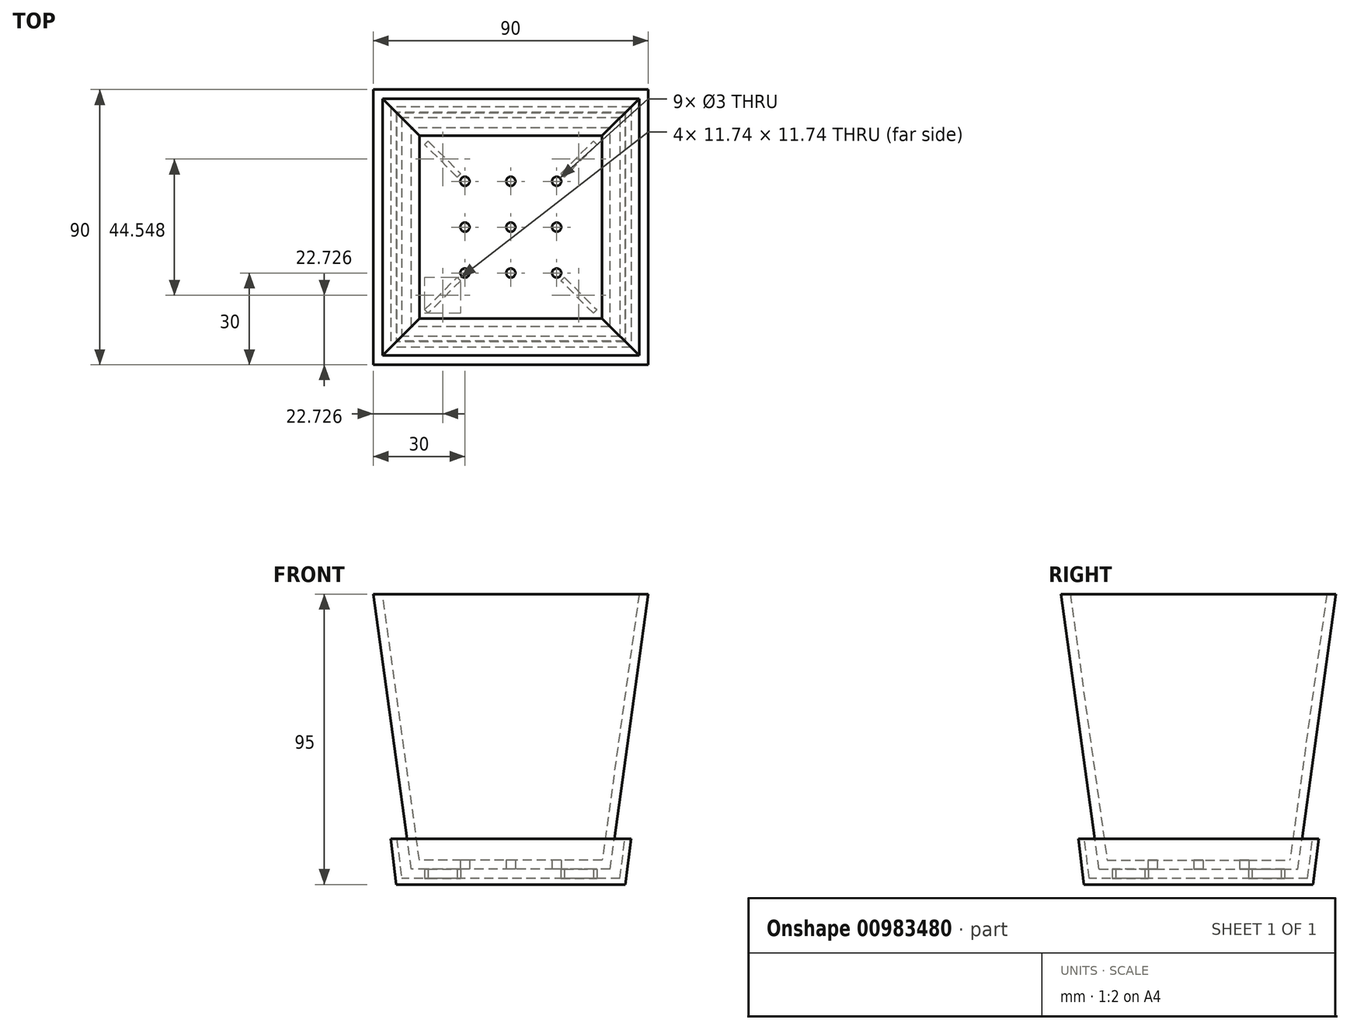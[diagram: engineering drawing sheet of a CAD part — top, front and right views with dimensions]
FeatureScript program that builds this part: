
annotation { "Feature Type Name" : "Feature", "Feature Type Description" : "" }
export const myFeature = defineFeature(function(context is Context, id is Id, definition is map)
    precondition{}
    {
        {
            var Q0;
            Q0=qCreatedBy(makeId("Top.planeOp"),FACE);
            var sketch = newSketch(context, id + "F0", { "sketchPlane" : qUnion([Q0])});
            skLineSegment(sketch, "E0.bottom", {"start": v(32.5, -32.5) * mm, "end": v(-32.5, -32.5) * mm});
            skLineSegment(sketch, "E0.top", {"start": v(32.5, 32.5) * mm, "end": v(-32.5, 32.5) * mm});
            skLineSegment(sketch, "E0.left", {"start": v(32.5, -32.5) * mm, "end": v(32.5, 32.5) * mm});
            skLineSegment(sketch, "E0.right", {"start": v(-32.5, -32.5) * mm, "end": v(-32.5, 32.5) * mm});
            skSolve(sketch);
        }
        {
            var Q0;
            Q0=qCreatedBy(makeId("Top.planeOp"),FACE);
            cPlane(context, id + "F1", {"entities" : qUnion([Q0]), "cplaneType" : CPlaneType.OFFSET, "offset" : 90 * mm, "width" : 150 * mm, "height" : 150 * mm});
        }
        {
            var Q0;
            Q0=qCreatedBy(id+"F1.planeOp",FACE);
            var sketch = newSketch(context, id + "F2", { "sketchPlane" : qUnion([Q0])});
            skLineSegment(sketch, "E1.bottom", {"start": v(45, -45) * mm, "end": v(-45, -45) * mm});
            skLineSegment(sketch, "E1.top", {"start": v(45, 45) * mm, "end": v(-45, 45) * mm});
            skLineSegment(sketch, "E1.left", {"start": v(45, -45) * mm, "end": v(45, 45) * mm});
            skLineSegment(sketch, "E1.right", {"start": v(-45, -45) * mm, "end": v(-45, 45) * mm});
            skPoint(sketch, "E1.middle", {"position": v(0, 0) * mm});
            skSolve(sketch);
        }
        {
            var Q0;
            Q0=makeQuery(id+"F0.imprint","IMPRINT",FACE,{"disambiguationData":[TD([[makeQuery(id+"F0.imprint","IMPRINT",EDGE,{"derivedFrom":sQuery(id+"F0.wireOp",EDGE,"E0.bottom")}),-1.0]])]});
            var Q1;
            Q1=makeQuery(id+"F2.imprint","IMPRINT",FACE,{"disambiguationData":[TD([[makeQuery(id+"F2.imprint","IMPRINT",EDGE,{"derivedFrom":sQuery(id+"F2.wireOp",EDGE,"E1.bottom")}),-1.0]])]});
            loft(context, id + "F3", {"sheetProfilesArray" : [{ "sheetProfileEntities" : qUnion([Q0]) }, { "sheetProfileEntities" : qUnion([Q1]) }]});
        }
        {
            var Q0;
            Q0=makeQuery(id+"F3.opLoft","CAP_FACE",FACE,{"disambiguationData":[OSD([makeQuery(id+"F2.imprint","IMPRINT",FACE,{"disambiguationData":[TD([[makeQuery(id+"F2.imprint","IMPRINT",EDGE,{"derivedFrom":sQuery(id+"F2.wireOp",EDGE,"E1.bottom")}),-1.0]])]})])],"isStart":true});
            shell(context, id + "F4", {"entities" : qUnion([Q0]), "thickness" : 3 * mm});
        }
        {
            var Q0;
            Q0=qCreatedBy(makeId("Top.planeOp"),FACE);
            var sketch = newSketch(context, id + "F5", { "sketchPlane" : qUnion([Q0])});
            skCircle(sketch, "E2", {"center": v(-15, -15) * mm, "radius": 1.5 * mm});
            skCircle(sketch, "E3.0.1.0", {"center": v(-15, 0) * mm, "radius": 1.5 * mm});
            skCircle(sketch, "E3.0.2.0", {"center": v(-15, 15) * mm, "radius": 1.5 * mm});
            skCircle(sketch, "E3.1.0.0", {"center": v(0, -15) * mm, "radius": 1.5 * mm});
            skCircle(sketch, "E3.1.1.0", {"center": v(0, 0) * mm, "radius": 1.5 * mm});
            skCircle(sketch, "E3.1.2.0", {"center": v(0, 15) * mm, "radius": 1.5 * mm});
            skCircle(sketch, "E3.2.0.0", {"center": v(15, -15) * mm, "radius": 1.5 * mm});
            skCircle(sketch, "E3.2.1.0", {"center": v(15, 0) * mm, "radius": 1.5 * mm});
            skCircle(sketch, "E3.2.2.0", {"center": v(15, 15) * mm, "radius": 1.5 * mm});
            skLineSegment(sketch, "E3.direction1", {"start": v(-15, -15) * mm, "end": v(0, -15) * mm, "construction": true});
            skLineSegment(sketch, "E3.direction2", {"start": v(-15, -15) * mm, "end": v(-15, 0) * mm, "construction": true});
            skSolve(sketch);
        }
        {
            var Q0;
            Q0 = qSketchRegion(id + "F5", true);
            extrude(context, id + "F6", {"entities" : qUnion([Q0]), "operationType" : NewBodyOperationType.REMOVE, "endBound" : BoundingType.THROUGH_ALL, "depth" : 25 * mm, "offsetDistance" : 25 * mm});
        }
        {
            var Q0;
            Q0=qCreatedBy(makeId("Top.planeOp"),FACE);
            cPlane(context, id + "F7", {"entities" : qUnion([Q0]), "cplaneType" : CPlaneType.OFFSET, "offset" : 5 * mm, "oppositeDirection" : true, "width" : 150 * mm, "height" : 150 * mm});
        }
        {
            var Q0;
            Q0=qCreatedBy(id+"F7.planeOp",FACE);
            var sketch = newSketch(context, id + "F8", { "sketchPlane" : qUnion([Q0])});
            skLineSegment(sketch, "E4.bottom", {"start": v(37.5, 37.5) * mm, "end": v(-37.5, 37.5) * mm});
            skLineSegment(sketch, "E4.top", {"start": v(37.5, -37.5) * mm, "end": v(-37.5, -37.5) * mm});
            skLineSegment(sketch, "E4.left", {"start": v(37.5, 37.5) * mm, "end": v(37.5, -37.5) * mm});
            skLineSegment(sketch, "E4.right", {"start": v(-37.5, 37.5) * mm, "end": v(-37.5, -37.5) * mm});
            skPoint(sketch, "E4.middle", {"position": v(0, 0) * mm});
            skSolve(sketch);
        }
        {
            var Q0;
            Q0=qCreatedBy(id+"F7.planeOp",FACE);
            cPlane(context, id + "F9", {"entities" : qUnion([Q0]), "cplaneType" : CPlaneType.OFFSET, "offset" : 15 * mm, "width" : 150 * mm, "height" : 150 * mm});
        }
        {
            var Q0;
            Q0=qCreatedBy(id+"F9.planeOp",FACE);
            var sketch = newSketch(context, id + "F10", { "sketchPlane" : qUnion([Q0])});
            skLineSegment(sketch, "E5.bottom", {"start": v(39.3, 39.3) * mm, "end": v(-39.3, 39.3) * mm});
            skLineSegment(sketch, "E5.top", {"start": v(39.3, -39.3) * mm, "end": v(-39.3, -39.3) * mm});
            skLineSegment(sketch, "E5.left", {"start": v(39.3, 39.3) * mm, "end": v(39.3, -39.3) * mm});
            skLineSegment(sketch, "E5.right", {"start": v(-39.3, 39.3) * mm, "end": v(-39.3, -39.3) * mm});
            skPoint(sketch, "E5.middle", {"position": v(0, 0) * mm});
            skSolve(sketch);
        }
        {
            var Q1;
            Q1=makeQuery(id+"F10.imprint","IMPRINT",FACE,{"disambiguationData":[TD([[makeQuery(id+"F10.imprint","IMPRINT",EDGE,{"derivedFrom":sQuery(id+"F10.wireOp",EDGE,"E5.bottom")}),1.0]])]});
            var Q2;
            Q2=makeQuery(id+"F8.imprint","IMPRINT",FACE,{"disambiguationData":[TD([[makeQuery(id+"F8.imprint","IMPRINT",EDGE,{"derivedFrom":sQuery(id+"F8.wireOp",EDGE,"E4.bottom")}),1.0]])]});
            loft(context, id + "F11", {"sheetProfilesArray" : [{ "sheetProfileEntities" : qUnion([Q1]) }, { "sheetProfileEntities" : qUnion([Q2]) }]});
        }
        {
            var Q0;
            Q0=makeQuery(id+"F11.opLoft","CAP_FACE",FACE,{"disambiguationData":[OSD([makeQuery(id+"F10.imprint","IMPRINT",FACE,{"disambiguationData":[TD([[makeQuery(id+"F10.imprint","IMPRINT",EDGE,{"derivedFrom":sQuery(id+"F10.wireOp",EDGE,"E5.bottom")}),1.0]])]})])],"isStart":true});
            shell(context, id + "F12", {"entities" : qUnion([Q0]), "thickness" : 2 * mm});
        }
        {
            var Q0;
            Q0=makeQuery(id+"F12.opShell","OFFSET_FACE",FACE,{"disambiguationData":[OSD([makeQuery(id+"F8.imprint","IMPRINT",FACE,{"disambiguationData":[TD([[makeQuery(id+"F8.imprint","IMPRINT",EDGE,{"derivedFrom":sQuery(id+"F8.wireOp",EDGE,"E4.bottom")}),1.0]])]})])]});
            var sketch = newSketch(context, id + "F13", { "sketchPlane" : qUnion([Q0])});
            skLineSegment(sketch, "E6", {"start": v(-16.4, -17.54) * mm, "end": v(-27.01, -28.14) * mm});
            skLineSegment(sketch, "E7", {"start": v(-27.01, -28.14) * mm, "end": v(-28.14, -27.01) * mm});
            skLineSegment(sketch, "E8", {"start": v(-28.14, -27.01) * mm, "end": v(-17.54, -16.4) * mm});
            skLineSegment(sketch, "E9", {"start": v(-17.54, -16.4) * mm, "end": v(-16.4, -17.54) * mm});
            skLineSegment(sketch, "E10.1.0", {"start": v(28.14, -27.01) * mm, "end": v(27.01, -28.14) * mm});
            skLineSegment(sketch, "E10.1.1", {"start": v(27.01, -28.14) * mm, "end": v(16.4, -17.54) * mm});
            skLineSegment(sketch, "E10.1.2", {"start": v(17.54, -16.4) * mm, "end": v(28.14, -27.01) * mm});
            skLineSegment(sketch, "E10.1.3", {"start": v(16.4, -17.54) * mm, "end": v(17.54, -16.4) * mm});
            skLineSegment(sketch, "E10.2.0", {"start": v(27.01, 28.14) * mm, "end": v(28.14, 27.01) * mm});
            skLineSegment(sketch, "E10.2.1", {"start": v(28.14, 27.01) * mm, "end": v(17.54, 16.4) * mm});
            skLineSegment(sketch, "E10.2.2", {"start": v(16.4, 17.54) * mm, "end": v(27.01, 28.14) * mm});
            skLineSegment(sketch, "E10.2.3", {"start": v(17.54, 16.4) * mm, "end": v(16.4, 17.54) * mm});
            skLineSegment(sketch, "E10.3.0", {"start": v(-28.14, 27.01) * mm, "end": v(-27.01, 28.14) * mm});
            skLineSegment(sketch, "E10.3.1", {"start": v(-27.01, 28.14) * mm, "end": v(-16.4, 17.54) * mm});
            skLineSegment(sketch, "E10.3.2", {"start": v(-17.54, 16.4) * mm, "end": v(-28.14, 27.01) * mm});
            skLineSegment(sketch, "E10.3.3", {"start": v(-16.4, 17.54) * mm, "end": v(-17.54, 16.4) * mm});
            skPoint(sketch, "E10.center", {"position": v(0, 0) * mm});
            skSolve(sketch);
        }
        {
            var Q0;
            Q0 = qSketchRegion(id + "F13", true);
            extrude(context, id + "F14", {"entities" : qUnion([Q0]), "operationType" : NewBodyOperationType.ADD, "depth" : 3 * mm, "offsetDistance" : 25 * mm});
        }
    });
